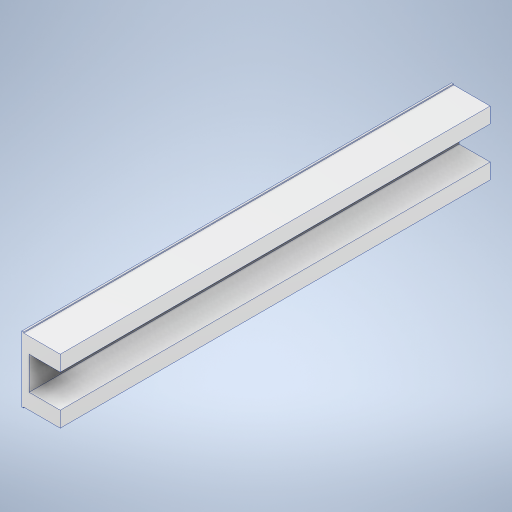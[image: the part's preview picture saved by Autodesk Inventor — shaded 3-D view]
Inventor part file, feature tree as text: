
AUTODESK INVENTOR PART (.ipt)
format: ipt  version: 2024 (Build 280153000, 153)  size: 340,992 bytes
history: native  units: mm
features: extrude x7, sketch x7, projected_geometry x3
ambient origin geometry x8: Origin, YZ Plane, XZ Plane, XY Plane, X Axis, Y Axis, Z Axis, Center Point
bodies: Solid1 (feature_tree)
feature tree (17):
  extrude  "Extrusion1"  Depth=160.0mm TaperAngle=0.0deg
  extrude  "Extrusion2"  Depth=25.0mm
  extrude  "Extrusion3"  Depth=45.0mm
  extrude  "Extrusion4"  Depth=4.0mm
  extrude  "Extrusion5"  Depth=36.0mm
  extrude  "Extrusion6"  Depth=150.0mm TaperAngle=0.0deg
  extrude  "Extrusion7"  Depth=470.0mm
  sketch  "Sketch1"  dims[d0=475.0mm d1=160.0mm d2=0.0mm]
  sketch  "Sketch2"  dims[d4=25.0mm d5=25.0mm]
  sketch  "Sketch3"  dims[d6=10.0mm d7=45.0mm]
  sketch  "Sketch4"  dims[d8=45.0mm d9=4.0mm]
  projected_geometry  "Projected Loop1"
  projected_geometry  "Projected Loop2"
  sketch  "Sketch5"  dims[d10=36.0mm d11=80.0mm]
  projected_geometry  "Projected Loop3"
  sketch  "Sketch6"  dims[d12=80.0mm d13=150.0mm d14=0.0mm]
  sketch  "Sketch7"  dims[d15=20.0mm d16=470.0mm d17=200.0mm d18=0.0mm d19=30.0mm d20=0.0mm d21=5.0mm d22=0.0mm d23=13.0mm d24=13.0mm d25=3.0mm d26=500.0mm d27=0.0mm d28=1.0mm d29=1.0mm d30=2.0mm d31=1000.0mm d32=0.0mm]
